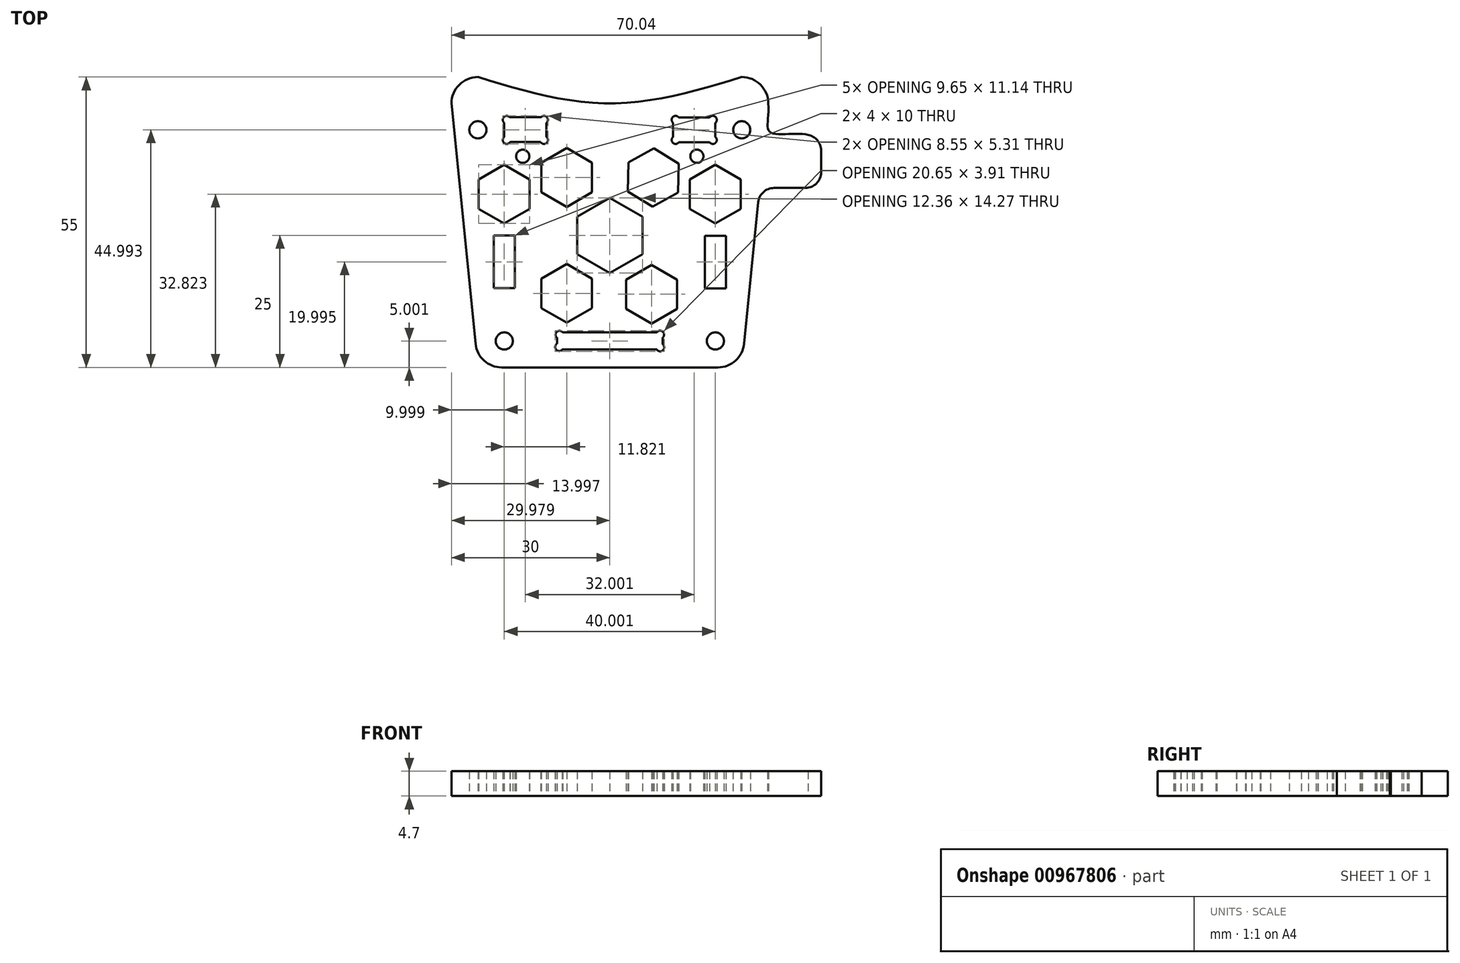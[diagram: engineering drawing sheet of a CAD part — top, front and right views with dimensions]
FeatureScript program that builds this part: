
annotation { "Feature Type Name" : "Feature", "Feature Type Description" : "" }
export const myFeature = defineFeature(function(context is Context, id is Id, definition is map)
    precondition{}
    {
        {
            var Q0;
            Q0=qCreatedBy(makeId("Top.planeOp"),FACE);
            var sketch = newSketch(context, id + "F0", { "sketchPlane" : qUnion([Q0])});
            skPoint(sketch, "E0.middle", {"position": v(0, 0) * mm});
            skCircle(sketch, "E1", {"center": v(-25, 20) * mm, "radius": 1.63 * mm});
            skCircle(sketch, "E2", {"center": v(25, 20) * mm, "radius": 1.63 * mm});
            skLineSegment(sketch, "E3.bottom", {"start": v(20, 22.35) * mm, "end": v(12, 22.35) * mm});
            skLineSegment(sketch, "E3.top", {"start": v(20, 17.65) * mm, "end": v(12, 17.65) * mm});
            skLineSegment(sketch, "E3.left", {"start": v(20, 22.35) * mm, "end": v(20, 17.65) * mm});
            skLineSegment(sketch, "E3.right", {"start": v(12, 22.35) * mm, "end": v(12, 17.65) * mm});
            skPoint(sketch, "E4", {"position": v(0, -20) * mm});
            skLineSegment(sketch, "E5.bottom", {"start": v(-10, -18.38) * mm, "end": v(10, -18.38) * mm});
            skLineSegment(sketch, "E5.top", {"start": v(-10, -21.63) * mm, "end": v(10, -21.63) * mm});
            skLineSegment(sketch, "E5.left", {"start": v(-10, -18.38) * mm, "end": v(-10, -21.63) * mm});
            skLineSegment(sketch, "E5.right", {"start": v(10, -18.38) * mm, "end": v(10, -21.63) * mm});
            skCircle(sketch, "E6", {"center": v(-16.5, 15) * mm, "radius": 1.25 * mm});
            skCircle(sketch, "E7", {"center": v(16.5, 15) * mm, "radius": 1.25 * mm});
            skCircle(sketch, "E8", {"center": v(20, -20) * mm, "radius": 1.63 * mm});
            skCircle(sketch, "E9", {"center": v(-20, -20) * mm, "radius": 1.63 * mm});
            skPoint(sketch, "E10.visualSharp", {"position": v(-30, 30) * mm});
            skArc(sketch, "E10.filletArc", {"start": v(-25, 30) * mm, "mid": v(-28.54, 28.54) * mm, "end": v(-30, 25) * mm});
            skPoint(sketch, "E11.visualSharp", {"position": v(30, 30) * mm});
            skArc(sketch, "E11.filletArc", {"start": v(30.03, 25.05) * mm, "mid": v(28.54, 28.56) * mm, "end": v(25, 30) * mm});
            skPoint(sketch, "E12.visualSharp", {"position": v(30, -30) * mm});
            skPoint(sketch, "E13.visualSharp", {"position": v(-30, -30) * mm});
            skCircle(sketch, "E14", {"center": v(19.52, 18.08) * mm, "radius": 0.75 * mm});
            skCircle(sketch, "E15", {"center": v(12.47, 18.08) * mm, "radius": 0.75 * mm});
            skCircle(sketch, "E16", {"center": v(12.47, 21.9) * mm, "radius": 0.75 * mm});
            skCircle(sketch, "E17", {"center": v(19.52, 21.9) * mm, "radius": 0.75 * mm});
            skLineSegment(sketch, "E18.bottom", {"start": v(-12, 22.4) * mm, "end": v(-20, 22.4) * mm});
            skLineSegment(sketch, "E18.top", {"start": v(-12, 17.7) * mm, "end": v(-20, 17.7) * mm});
            skLineSegment(sketch, "E18.left", {"start": v(-12, 22.4) * mm, "end": v(-12, 17.7) * mm});
            skLineSegment(sketch, "E18.right", {"start": v(-20, 22.4) * mm, "end": v(-20, 17.7) * mm});
            skCircle(sketch, "E19", {"center": v(-12.48, 18.08) * mm, "radius": 0.75 * mm});
            skCircle(sketch, "E20", {"center": v(-19.53, 18.08) * mm, "radius": 0.75 * mm});
            skCircle(sketch, "E21", {"center": v(-19.53, 21.9) * mm, "radius": 0.75 * mm});
            skCircle(sketch, "E22", {"center": v(-12.48, 21.9) * mm, "radius": 0.75 * mm});
            skCircle(sketch, "E23.cCircle", {"center": v(0, 0) * mm, "radius": 6.18 * mm, "construction": true});
            skLineSegment(sketch, "E23.0", {"start": v(6.18, 3.57) * mm, "end": v(6.18, -3.57) * mm});
            skLineSegment(sketch, "E23.1", {"start": v(6.18, -3.57) * mm, "end": v(0, -7.14) * mm});
            skLineSegment(sketch, "E23.2", {"start": v(0, -7.14) * mm, "end": v(-6.18, -3.57) * mm});
            skLineSegment(sketch, "E23.3", {"start": v(-6.18, -3.57) * mm, "end": v(-6.18, 3.57) * mm});
            skLineSegment(sketch, "E23.4", {"start": v(-6.18, 3.57) * mm, "end": v(0, 7.14) * mm});
            skLineSegment(sketch, "E23.5", {"start": v(0, 7.14) * mm, "end": v(6.18, 3.57) * mm});
            skPoint(sketch, "E23.0.midPoint", {"position": v(6.18, 0) * mm});
            skCircle(sketch, "E24.cCircle", {"center": v(-8.18, -10.97) * mm, "radius": 4.83 * mm, "construction": true});
            skLineSegment(sketch, "E24.0", {"start": v(-3.35, -8.19) * mm, "end": v(-3.35, -13.76) * mm});
            skLineSegment(sketch, "E24.1", {"start": v(-3.35, -13.76) * mm, "end": v(-8.18, -16.54) * mm});
            skLineSegment(sketch, "E24.2", {"start": v(-8.18, -16.54) * mm, "end": v(-13, -13.76) * mm});
            skLineSegment(sketch, "E24.3", {"start": v(-13, -13.76) * mm, "end": v(-13, -8.19) * mm});
            skLineSegment(sketch, "E24.4", {"start": v(-13, -8.19) * mm, "end": v(-8.18, -5.4) * mm});
            skLineSegment(sketch, "E24.5", {"start": v(-8.18, -5.4) * mm, "end": v(-3.35, -8.19) * mm});
            skPoint(sketch, "E24.0.midPoint", {"position": v(-3.35, -10.97) * mm});
            skLineSegment(sketch, "E25", {"start": v(-30, 25) * mm, "end": v(-25.45, -20.5) * mm});
            skLineSegment(sketch, "E26", {"start": v(-20.48, -25) * mm, "end": v(20.48, -25) * mm});
            skLineSegment(sketch, "E27", {"start": v(25.45, -20.5) * mm, "end": v(28.13, 6.28) * mm});
            skPoint(sketch, "E28.visualSharp", {"position": v(-25, -25) * mm});
            skArc(sketch, "E28.filletArc", {"start": v(-25.45, -20.5) * mm, "mid": v(-23.83, -23.7) * mm, "end": v(-20.48, -25) * mm});
            skPoint(sketch, "E29.visualSharp", {"position": v(25, -25) * mm});
            skArc(sketch, "E29.filletArc", {"start": v(20.48, -25) * mm, "mid": v(23.83, -23.7) * mm, "end": v(25.45, -20.5) * mm});
            skCircle(sketch, "E30.cCircle", {"center": v(8.25, 10.98) * mm, "radius": 4.77 * mm, "construction": true});
            skLineSegment(sketch, "E30.0", {"start": v(13.09, 13.61) * mm, "end": v(12.95, 8.1) * mm});
            skLineSegment(sketch, "E30.1", {"start": v(12.95, 8.1) * mm, "end": v(8.12, 5.47) * mm});
            skLineSegment(sketch, "E30.2", {"start": v(8.12, 5.47) * mm, "end": v(3.42, 8.34) * mm});
            skLineSegment(sketch, "E30.3", {"start": v(3.42, 8.34) * mm, "end": v(3.55, 13.84) * mm});
            skLineSegment(sketch, "E30.4", {"start": v(3.55, 13.84) * mm, "end": v(8.38, 16.48) * mm});
            skLineSegment(sketch, "E30.5", {"start": v(8.38, 16.48) * mm, "end": v(13.09, 13.61) * mm});
            skPoint(sketch, "E30.0.midPoint", {"position": v(13.02, 10.86) * mm});
            skCircle(sketch, "E31.cCircle", {"center": v(-8.18, 10.98) * mm, "radius": 4.83 * mm, "construction": true});
            skLineSegment(sketch, "E31.0", {"start": v(-3.35, 13.76) * mm, "end": v(-3.35, 8.19) * mm});
            skLineSegment(sketch, "E31.1", {"start": v(-3.35, 8.19) * mm, "end": v(-8.18, 5.4) * mm});
            skLineSegment(sketch, "E31.2", {"start": v(-8.18, 5.4) * mm, "end": v(-13, 8.19) * mm});
            skLineSegment(sketch, "E31.3", {"start": v(-13, 8.19) * mm, "end": v(-13, 13.76) * mm});
            skLineSegment(sketch, "E31.4", {"start": v(-13, 13.76) * mm, "end": v(-8.18, 16.55) * mm});
            skLineSegment(sketch, "E31.5", {"start": v(-8.18, 16.55) * mm, "end": v(-3.35, 13.76) * mm});
            skPoint(sketch, "E31.0.midPoint", {"position": v(-3.35, 10.98) * mm});
            skCircle(sketch, "E32", {"center": v(9.54, -18.79) * mm, "radius": 0.75 * mm});
            skCircle(sketch, "E33", {"center": v(-9.53, -18.81) * mm, "radius": 0.75 * mm});
            skCircle(sketch, "E34", {"center": v(-9.6, -21.15) * mm, "radius": 0.75 * mm});
            skCircle(sketch, "E35", {"center": v(9.55, -21.2) * mm, "radius": 0.75 * mm});
            skFitSpline(sketch, "E36", {"points": [v(-25, 30) * mm, v(0, 25) * mm, v(25, 30) * mm], "startDerivative": vector(50, -15) * mm, "endDerivative": vector(50, 15) * mm});
            skPoint(sketch, "E37.visualSharp", {"position": v(-8.18, 16.55) * mm});
            skLineSegment(sketch, "E37.filletArc", {"start": v(-8.18, 16.55) * mm, "end": v(-8.18, 16.55) * mm});
            skPoint(sketch, "E38.visualSharp", {"position": v(-3.35, 13.76) * mm});
            skLineSegment(sketch, "E38.filletArc", {"start": v(-3.35, 13.76) * mm, "end": v(-3.35, 13.76) * mm});
            skPoint(sketch, "E39.visualSharp", {"position": v(-3.35, 8.19) * mm});
            skLineSegment(sketch, "E39.filletArc", {"start": v(-3.35, 8.19) * mm, "end": v(-3.35, 8.19) * mm});
            skPoint(sketch, "E40.visualSharp", {"position": v(-8.18, 5.4) * mm});
            skLineSegment(sketch, "E40.filletArc", {"start": v(-8.18, 5.4) * mm, "end": v(-8.18, 5.4) * mm});
            skPoint(sketch, "E41.visualSharp", {"position": v(-13, 8.19) * mm});
            skLineSegment(sketch, "E41.filletArc", {"start": v(-13, 8.19) * mm, "end": v(-13, 8.19) * mm});
            skPoint(sketch, "E42.visualSharp", {"position": v(-13, 13.76) * mm});
            skLineSegment(sketch, "E42.filletArc", {"start": v(-13, 13.76) * mm, "end": v(-13, 13.76) * mm});
            skLineSegment(sketch, "E43.bottom", {"start": v(22, -10.05) * mm, "end": v(18, -10.05) * mm});
            skLineSegment(sketch, "E43.top", {"start": v(22, -0.05) * mm, "end": v(18, -0.05) * mm});
            skLineSegment(sketch, "E43.left", {"start": v(22, -10.05) * mm, "end": v(22, -0.05) * mm});
            skLineSegment(sketch, "E43.right", {"start": v(18, -10.05) * mm, "end": v(18, -0.05) * mm});
            skPoint(sketch, "E43.middle", {"position": v(20, -5.05) * mm});
            skLineSegment(sketch, "E44.bottom", {"start": v(-18, -10) * mm, "end": v(-22, -10) * mm});
            skLineSegment(sketch, "E44.top", {"start": v(-18, 0) * mm, "end": v(-22, 0) * mm});
            skLineSegment(sketch, "E44.left", {"start": v(-18, -10) * mm, "end": v(-18, 0) * mm});
            skLineSegment(sketch, "E44.right", {"start": v(-22, -10) * mm, "end": v(-22, 0) * mm});
            skPoint(sketch, "E44.middle", {"position": v(-20, -5) * mm});
            skCircle(sketch, "E45.cCircle", {"center": v(-20, 7.82) * mm, "radius": 4.83 * mm, "construction": true});
            skLineSegment(sketch, "E45.0", {"start": v(-15.18, 10.6) * mm, "end": v(-15.18, 5.04) * mm});
            skLineSegment(sketch, "E45.1", {"start": v(-15.18, 5.04) * mm, "end": v(-20, 2.25) * mm});
            skLineSegment(sketch, "E45.2", {"start": v(-20, 2.25) * mm, "end": v(-24.83, 5.04) * mm});
            skLineSegment(sketch, "E45.3", {"start": v(-24.83, 5.04) * mm, "end": v(-24.83, 10.6) * mm});
            skLineSegment(sketch, "E45.4", {"start": v(-24.83, 10.6) * mm, "end": v(-20, 13.4) * mm});
            skLineSegment(sketch, "E45.5", {"start": v(-20, 13.4) * mm, "end": v(-15.18, 10.6) * mm});
            skPoint(sketch, "E45.0.midPoint", {"position": v(-15.18, 7.82) * mm});
            skPoint(sketch, "E46", {"position": v(-20, 0) * mm});
            skPoint(sketch, "E47", {"position": v(27.73, 2.25) * mm});
            skCircle(sketch, "E48.cCircle", {"center": v(20, 7.82) * mm, "radius": 4.83 * mm, "construction": true});
            skLineSegment(sketch, "E48.0", {"start": v(24.83, 10.6) * mm, "end": v(24.83, 5.04) * mm});
            skLineSegment(sketch, "E48.1", {"start": v(24.83, 5.04) * mm, "end": v(20, 2.25) * mm});
            skLineSegment(sketch, "E48.2", {"start": v(20, 2.25) * mm, "end": v(15.17, 5.04) * mm});
            skLineSegment(sketch, "E48.3", {"start": v(15.17, 5.04) * mm, "end": v(15.17, 10.6) * mm});
            skLineSegment(sketch, "E48.4", {"start": v(15.17, 10.6) * mm, "end": v(20, 13.4) * mm});
            skLineSegment(sketch, "E48.5", {"start": v(20, 13.4) * mm, "end": v(24.83, 10.6) * mm});
            skPoint(sketch, "E48.0.midPoint", {"position": v(24.83, 7.82) * mm});
            skPoint(sketch, "E49", {"position": v(20, -0.05) * mm});
            skLineSegment(sketch, "E50.bottom", {"start": v(31.11, 8.99) * mm, "end": v(37.04, 8.99) * mm});
            skLineSegment(sketch, "E50.right", {"start": v(40.04, 11.99) * mm, "end": v(40.04, 16.08) * mm});
            skPoint(sketch, "E51.newPointA", {"position": v(30, 25) * mm});
            skArc(sketch, "E51.filletArc", {"start": v(31.11, 8.99) * mm, "mid": v(29.1, 8.2) * mm, "end": v(28.13, 6.28) * mm});
            skPoint(sketch, "E52.visualSharp", {"position": v(40.04, 8.99) * mm});
            skArc(sketch, "E52.filletArc", {"start": v(37.04, 8.99) * mm, "mid": v(39.16, 9.86) * mm, "end": v(40.04, 11.99) * mm});
            skPoint(sketch, "E53.visualSharp", {"position": v(40.04, 21.9) * mm});
            skArc(sketch, "E53.filletArc", {"start": v(40.04, 16.08) * mm, "mid": v(39.34, 18.02) * mm, "end": v(37.55, 19.04) * mm});
            skFitSpline(sketch, "E54", {"points": [v(37.55, 19.04) * mm, v(30.5, 19.49) * mm, v(30.03, 25.05) * mm], "startDerivative": vector(-10.27, 3.2) * mm, "endDerivative": vector(-1.49, 19.34) * mm});
            skCircle(sketch, "E55", {"center": v(0, 44.14) * mm, "radius": 2.25 * mm});
            skCircle(sketch, "E56", {"center": v(0, 44.14) * mm, "radius": 2.5 * mm});
            skCircle(sketch, "E57", {"center": v(0, -40.18) * mm, "radius": 2.25 * mm});
            skCircle(sketch, "E58", {"center": v(0, -40.18) * mm, "radius": 2.5 * mm});
            skCircle(sketch, "E59.cCircle", {"center": v(7.92, -11.14) * mm, "radius": 4.83 * mm, "construction": true});
            skLineSegment(sketch, "E59.0", {"start": v(12.74, -8.36) * mm, "end": v(12.74, -13.93) * mm});
            skLineSegment(sketch, "E59.1", {"start": v(12.74, -13.93) * mm, "end": v(7.92, -16.71) * mm});
            skLineSegment(sketch, "E59.2", {"start": v(7.92, -16.71) * mm, "end": v(3.1, -13.93) * mm});
            skLineSegment(sketch, "E59.3", {"start": v(3.1, -13.93) * mm, "end": v(3.1, -8.36) * mm});
            skLineSegment(sketch, "E59.4", {"start": v(3.1, -8.36) * mm, "end": v(7.92, -5.57) * mm});
            skLineSegment(sketch, "E59.5", {"start": v(7.92, -5.57) * mm, "end": v(12.74, -8.36) * mm});
            skPoint(sketch, "E59.0.midPoint", {"position": v(12.74, -11.14) * mm});
            skPoint(sketch, "E60", {"position": v(3.1, 5.35) * mm});
            skSolve(sketch);
        }
        {
            var Q0;
            Q0=makeQuery(id+"F0.imprint","IMPRINT",FACE,{"disambiguationData":[TD([[makeQuery(id+"F0.imprint","IMPRINT",EDGE,{"derivedFrom":sQuery(id+"F0.wireOp",EDGE,"E1")}),-1.0]])]});
            var Q1;
            Q1=makeQuery(id+"F0.imprint","IMPRINT",FACE,{"disambiguationData":[TD([[makeQuery(id+"F0.imprint","IMPRINT",EDGE,{"derivedFrom":sQuery(id+"F0.wireOp",EDGE,"E2")}),-1.0]])]});
            var Q2;
            {var subQ5=sQuery(id+"F0.wireOp",EDGE,"E50.right");Q2=makeQuery(id+"F0.imprint","IMPRINT",FACE,{"disambiguationData":[TD([[makeQuery(id+"F0.imprint","IMPRINT",EDGE,{"derivedFrom":subQ5}),1.0]])]});}
            extrude(context, id + "F1", {"entities" : qUnion([Q0, Q1, Q2]), "depth" : 4.7 * mm, "offsetDistance" : 25 * mm});
        }
    });
